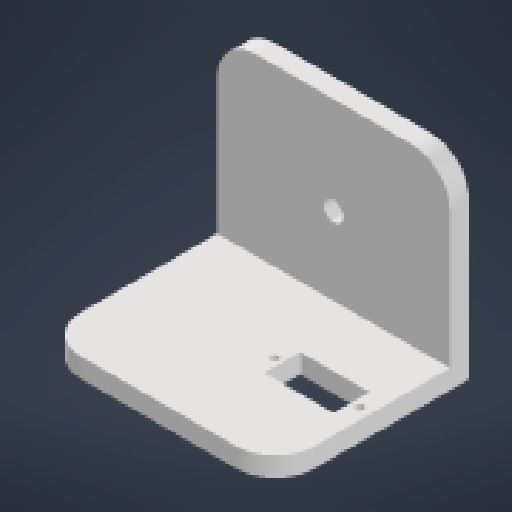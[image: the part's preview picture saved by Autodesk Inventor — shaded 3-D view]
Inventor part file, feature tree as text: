
AUTODESK INVENTOR PART (.ipt)
format: ipt  version: 2023 (Build 270158000, 158)  size: 163,328 bytes
history: native  units: in
note: dims shown in document units (in); Inventor stores cm internally (conversion verified against a paired STEP export)
features: reference x10, extrude x5, sketch x5, other x3, fillet x1, plane x1
ambient origin geometry x8: Origin, YZ Plane, XZ Plane, XY Plane, X Axis, Y Axis, Z Axis, Center Point
bodies: Solid1 (feature_tree)
feature tree (25):
  extrude  "Extrusion1"  Depth=2.5in
  extrude  "Extrusion2"  Depth=0.25in
  fillet  "Fillet1"  Radius=2.25in
  extrude  "Extrusion3"  Depth=0.25in
  extrude  "Extrusion4"  Depth=0.892in
  sketch  "Sketch5"  dims[d12=1.0in d13=0.0in d14=0.19in d18=1.0in d19=0.0in]
  plane  "Work Plane1"
  extrude  "Extrusion5"  Depth=1.0in
  sketch  "Sketch1"  dims[d0=3.0in d1=2.5in]
  sketch  "Sketch2"  dims[d2=0.25in d3=0.0in d4=0.25in d5=2.25in d6=0.0in]
  sketch  "Sketch3"  dims[d7=0.5in d8=0.25in]
  sketch  "Sketch4"  dims[d9=1.0in d10=0.0in d11=0.892in]
  reference  "Reference1"
  reference  "Reference2"
  reference  "Reference3"
  reference  "Reference4"
  reference  "Reference5"
  reference  "Reference6"
  reference  "Reference7"
  reference  "Reference8"
  reference  "Reference9"
  reference  "Reference10"
  parser-record x1  (decoder bookkeeping rows leaked as tree rows — omitted from the tree; the rows remain in map.json)
  other  "Gripper.iam"
  other  "Servo:1"
note: 1 file-system path scrubbed to <path> (originals preserved in map.json)
